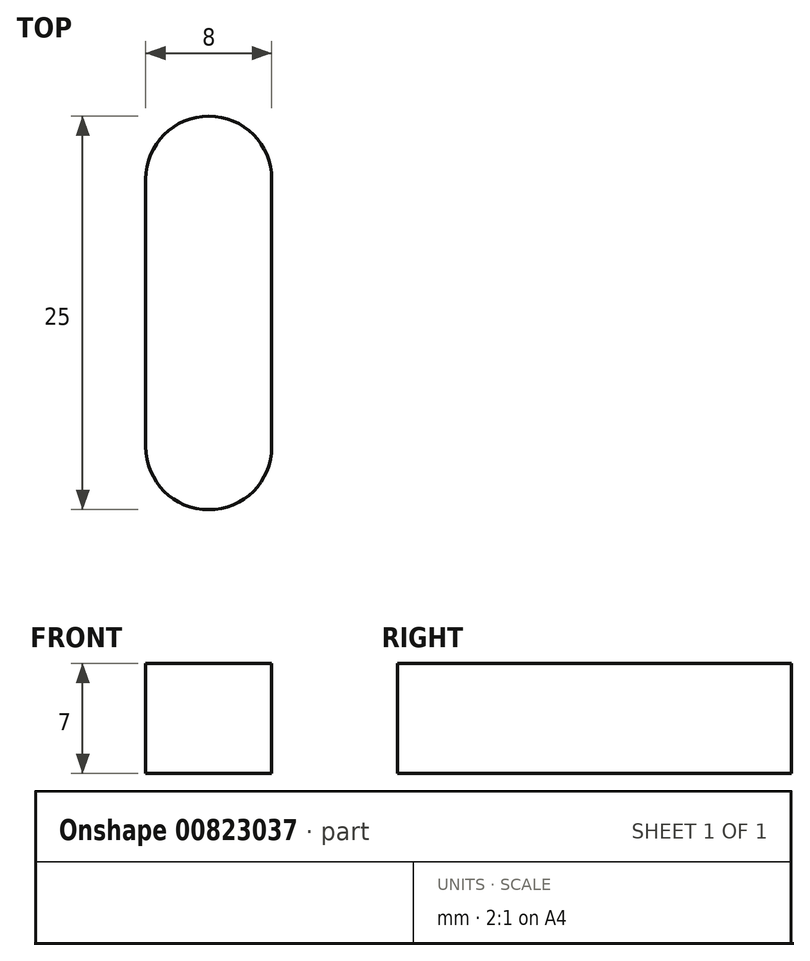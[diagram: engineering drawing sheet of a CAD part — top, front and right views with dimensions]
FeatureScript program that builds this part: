
annotation { "Feature Type Name" : "Feature", "Feature Type Description" : "" }
export const myFeature = defineFeature(function(context is Context, id is Id, definition is map)
    precondition{}
    {
        {
            var Q0;
            Q0=qCreatedBy(makeId("Top.planeOp"),FACE);
            var sketch = newSketch(context, id + "F0", { "sketchPlane" : qUnion([Q0])});
            skLineSegment(sketch, "E0.left", {"start": v(4, 8.5) * mm, "end": v(4, -8.5) * mm});
            skLineSegment(sketch, "E0.right", {"start": v(-4, 8.5) * mm, "end": v(-4, -8.5) * mm});
            skPoint(sketch, "E0.middle", {"position": v(0, 0) * mm});
            skArc(sketch, "E1", {"start": v(4, 8.5) * mm, "mid": v(0, 12.5) * mm, "end": v(-4, 8.5) * mm});
            skArc(sketch, "E2", {"start": v(-4, -8.5) * mm, "mid": v(0, -12.5) * mm, "end": v(4, -8.5) * mm});
            skSolve(sketch);
        }
        {
            var Q0;
            Q0=qSketchRegion(id+"F0",true);
            extrude(context, id + "F1", {"entities" : qUnion([Q0]), "depth" : 7 * mm, "offsetDistance" : 25 * mm});
        }
    });
